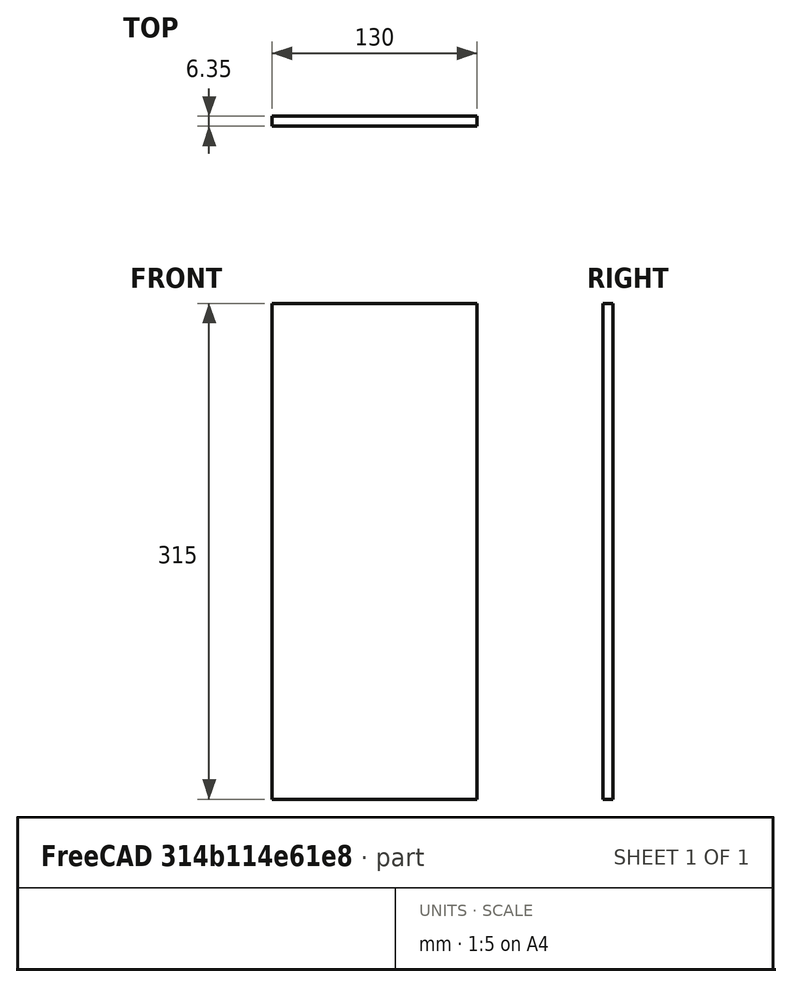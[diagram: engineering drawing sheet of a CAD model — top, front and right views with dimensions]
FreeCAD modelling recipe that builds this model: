
FCSTD DOCUMENT  (FreeCAD 1.0R39109 (Git))
Label: Integrated PiTrac
License: All rights reserved
LicenseURL: http://en.wikipedia.org/wiki/All_rights_reserved
objects: App::Link×14, App::Part×2, Sketcher::SketchObject×1, PartDesign::Pad×1, PartDesign::Body×1
note: 6 computed .brp shape members not serialized (recipe doc carries the construction recipe); baked Part::Feature solids carry a one-line shape summary decoded from their .brp
EXTERNAL_REF file=../Master Document.FCStd obj=Spreadsheet
EXTERNAL_REF file=../PiTracComputeBoard/PiTracComputeBoard.FCStd obj=p2AP_PCBModel
EXTERNAL_REF file=../Tower/Tower.FCStd obj=Part
EXTERNAL_REF file=../Pi-Camera-Mounts/Camera Mount - Bottom.FCStd obj=Part
EXTERNAL_REF file=../LED-Array-Strobe-Light-Mount/LED Light Mount.FCStd obj=Part
EXTERNAL_REF file=Pi HQ Camera.FCStd obj=Raspberry_Pi_HQ_Camera_with_cs_mount_lens_v3
EXTERNAL_REF file=Cree LED Lens.FCStd obj=Scale
EXTERNAL_REF file=../Pi-Camera-Mounts/Camera Mount - Top Variation (Cam1).FCStd obj=Part
EXTERNAL_REF file=../Pi-Camera-Light-Filter-Holder/Pi Cam Filter Holder v1.00.FCStd obj=Part
EXTERNAL_REF file=../BaseBox/BaseBox.FCStd obj=Part
EXTERNAL_REF file=LRS-150 Meanwell.FCStd obj=LRS_150
EXTERNAL_REF file=C14 Panel Mount Power Plug Adapter w Fuse - JR-101-1F.FCStd obj=JR_101_1F
EXTERNAL_REF file=../CaseCover/CaseCover.FCStd obj=Part

FEATURE [App::Part] Part  label="Integrated Part"
  Origin = -> Origin
FEATURE [App::Link] Link  label="Monitor Chassis Parameters"
  LinkPlacement = pos=(-5.9,7.03335e-07,0) rot=(0,0,1;0rad)
  LinkedObject = -> <external ../Master Document.FCStd>#Spreadsheet
  Placement = pos=(-5.9,7.03335e-07,0) rot=(0,0,1;0rad)
FEATURE [App::Link] Link002  label="p2AP-PCBModel"
  LinkPlacement = pos=(-49.1,-7.80001,20.1) rot=(1,0,0;1.5708rad)
  LinkedObject = -> <external ../PiTracComputeBoard/PiTracComputeBoard.FCStd>#p2AP_PCBModel
  Placement = pos=(-49.1,-7.80001,20.1) rot=(1,0,0;1.5708rad)
FEATURE [App::Link] Link003  label="Tower Part"
  LinkPlacement = pos=(1.5,3.6,0) rot=(0,0,1;0rad)
  LinkedObject = -> <external ../Tower/Tower.FCStd>#Part
  Placement = pos=(1.5,3.6,0) rot=(0,0,1;0rad)
FEATURE [App::Link] Link004  label="Botom Camera Mount Object"
  LinkPlacement = pos=(1.5,11.8,24.2) rot=(1,0,0;1.5708rad)
  LinkedObject = -> <external ../Pi-Camera-Mounts/Camera Mount - Bottom.FCStd>#Part
  Placement = pos=(1.5,11.8,24.2) rot=(1,0,0;1.5708rad)
FEATURE [App::Link] Link005  label="LED Light Mount Object"
  LinkPlacement = pos=(1.1,50.9,87.4) rot=(1,0,0;1.5708rad)
  LinkedObject = -> <external ../LED-Array-Strobe-Light-Mount/LED Light Mount.FCStd>#Part
  Placement = pos=(1.1,50.9,87.4) rot=(1,0,0;1.5708rad)
FEATURE [App::Link] Link006  label="Bottom Raspberry Pi HQ Camera with cs mount lens v014"
  LinkPlacement = pos=(-17.4,39.4031,23.6917) rot=(1,0,0;0.261799rad)
  LinkedObject = -> <external Pi HQ Camera.FCStd>#Raspberry_Pi_HQ_Camera_with_cs_mount_lens_v3
  Placement = pos=(-17.4,39.4031,23.6917) rot=(1,0,0;0.261799rad)
FEATURE [App::Link] Link007  label="LED Lens Scale"
  LinkPlacement = pos=(0,45.6236,128.978) rot=(1,0,0;0.261799rad)
  LinkedObject = -> <external Cree LED Lens.FCStd>#Scale
  Placement = pos=(0,45.6236,128.978) rot=(1,0,0;0.261799rad)
FEATURE [App::Link] Link008  label="Camera Mount - Top Object"
  LinkPlacement = pos=(15.7,56.8,199.2) rot=(1,0,0;1.5708rad)
  LinkedObject = -> <external ../Pi-Camera-Mounts/Camera Mount - Top Variation (Cam1).FCStd>#Part
  Placement = pos=(15.7,56.8,199.2) rot=(1,0,0;1.5708rad)
FEATURE [App::Link] Link009  label="Raspberry Pi HQ Camera with cs mount lens v014"
  LinkPlacement = pos=(-17.6,24.9301,203.909) rot=(-1,0,0;0.523599rad)
  LinkedObject = -> <external Pi HQ Camera.FCStd>#Raspberry_Pi_HQ_Camera_with_cs_mount_lens_v3
  Placement = pos=(-17.6,24.9301,203.909) rot=(-1,0,0;0.523599rad)
FEATURE [App::Link] Link010  label="Filter Holder Part"
  LinkPlacement = pos=(0.6,83.4834,56.5158) rot=(1,0,0;0.261799rad)
  LinkedObject = -> <external ../Pi-Camera-Light-Filter-Holder/Pi Cam Filter Holder v1.00.FCStd>#Part
  Placement = pos=(0.6,83.4834,56.5158) rot=(1,0,0;0.261799rad)
FEATURE [App::Link] Link011  label="BaseBox Part"
  LinkPlacement = pos=(101.6,36.6,-51) rot=(0,0,1;3.14159rad)
  LinkedObject = -> <external ../BaseBox/BaseBox.FCStd>#Part
  Placement = pos=(101.6,36.6,-51) rot=(0,0,1;3.14159rad)
FEATURE [App::Link] Link012  label="LRS-154"
  LinkPlacement = pos=(18,9.4,-50.9) rot=(-0.57735,0.57735,0.57735;4.18879rad)
  LinkedObject = -> <external LRS-150 Meanwell.FCStd>#LRS_150
  Placement = pos=(18,9.4,-50.9) rot=(-0.57735,0.57735,0.57735;4.18879rad)
FEATURE [Sketcher::SketchObject] Sketch  label="Shank Shield Sketch"
  ArcFitTolerance = 1e-06
  AttachmentSupport = -> [XZ_Plane002]
  FullyConstrained = false
  MakeInternals = false
  MapMode = 5
  Placement = pos=(0,0,0) rot=(1,0,0;1.5708rad)
  expr: Constraints[8] = <<Monitor Chassis Parameters>>.GSShankShieldWidth
  expr: Constraints[9] = <<Monitor Chassis Parameters>>.GSShankShieldHeight
  sketch-geometry (4):
    g0: LineSegment StartX=68.4149 StartY=-76.5925 StartZ=0 EndX=68.4149 EndY=238.407 EndZ=0
    g1: LineSegment StartX=68.4149 StartY=238.407 StartZ=0 EndX=-61.5851 EndY=238.407 EndZ=0
    g2: LineSegment StartX=-61.5851 StartY=238.407 StartZ=0 EndX=-61.5851 EndY=-76.5925 EndZ=0
    g3: LineSegment StartX=-61.5851 StartY=-76.5925 StartZ=0 EndX=68.4149 EndY=-76.5925 EndZ=0
  constraints (10):
    c: Coincident(g0,g1)
    c: Coincident(g1,g2)
    c: Coincident(g2,g3)
    c: Coincident(g3,g0)
    c: Vertical(g0)
    c: Vertical(g2)
    c: Horizontal(g1)
    c: Horizontal(g3)
    c: DistanceX(g1,g0) = 130
    c: DistanceY(g0,g0) = 315
FEATURE [PartDesign::Pad] Pad  label="Shank Shield Pad"
  Direction = (0,-1,2e-16)
  Length = 6.35
  Length2 = 10
  Placement = pos=(0,0,0) rot=(1,0,0;1.5708rad)
  Profile = -> Sketch
  ReferenceAxis = -> Sketch [N_Axis]
  Suppressed = false
  Type = 0
  expr: Length = <<Monitor Chassis Parameters>>.GSShankShieldThickness
FEATURE [PartDesign::Body] Body  label="Shank Shield Body"
  AllowCompound = false
  Group = -> [Sketch,Pad]
  Origin = -> Origin002
  Tip = -> Pad
FEATURE [App::Part] Part001  label="Shank Shield Part"
  Group = -> [Body]
  Origin = -> Origin001
  Placement = pos=(0,112.4,25.5) rot=(0,0,1;0rad)
FEATURE [App::Link] Link013  label="JR-101-1F008"
  LinkPlacement = pos=(-98.4001,76.6999,-31.4001) rot=(0.57735,-0.57735,-0.57735;2.0944rad)
  LinkedObject = -> <external C14 Panel Mount Power Plug Adapter w Fuse - JR-101-1F.FCStd>#JR_101_1F
  Placement = pos=(-98.4001,76.6999,-31.4001) rot=(0.57735,-0.57735,-0.57735;2.0944rad)
FEATURE [App::Link] Link014  label="Case Cover Part"
  LinkPlacement = pos=(2.9,27.2,-5.1) rot=(0,0,1;3.14159rad)
  LinkedObject = -> <external ../CaseCover/CaseCover.FCStd>#Part
  Placement = pos=(2.9,27.2,-5.1) rot=(0,0,1;3.14159rad)

RESOLVED EXTERNAL PARTS (link-assembly join: the EXTERNAL_REF files above that resolve inside this repo's crawl, each included once):
---- part ../BaseBox/BaseBox.FCStd = doc fcstd_369560cff5c8 (88262 chars; too large to inline — full recipe in that document) ----
---- part ../CaseCover/CaseCover.FCStd = doc fcstd_a5773d0cd6bc ----
FCSTD DOCUMENT  (FreeCAD 1.0R39109 (Git))
Label: CaseCover
License: All rights reserved
LicenseURL: http://en.wikipedia.org/wiki/All_rights_reserved
objects: Sketcher::SketchObject×17, PartDesign::Pad×9, PartDesign::Plane×8, PartDesign::Pocket×8, PartDesign::LinearPattern×3, PartDesign::Mirrored×2, PartDesign::Body×2, App::Link×1, App::Part×1
note: 105 computed .brp shape members not serialized (recipe doc carries the construction recipe); baked Part::Feature solids carry a one-line shape summary decoded from their .brp
EXTERNAL_REF file=../Master Document.FCStd obj=Spreadsheet

FEATURE [App::Link] Link  label="Monitor Chassis Parameters"
  LinkedObject = -> <external ../Master Document.FCStd>#Spreadsheet
FEATURE [Sketcher::SketchObject] Sketch  label="Lower Case Wall Base Sketch"
  ArcFitTolerance = 1e-06
  AttachmentSupport = -> [XY_Plane001]
  FullyConstrained = true
  MakeInternals = false
  MapMode = 5
  expr: Constraints[11] = 0.5 * <<Monitor Chassis Parameters>>.GSCaseWallInnerDepth
  expr: Constraints[12] = <<Monitor Chassis Parameters>>.GSCaseWallInnerWidth
  expr: Constraints[13] = <<Monitor Chassis Parameters>>.GSCaseWallThickness
  expr: Constraints[14] = 0.5 * <<Monitor Chassis Parameters>>.GSCaseWallInnerWidth
  expr: Constraints[23] = <<Monitor Chassis Parameters>>.GSCaseWallThickness
  expr: Constraints[24] = <<Monitor Chassis Parameters>>.GSCaseWallThickness
  expr: Constraints[9] = <<Monitor Chassis Parameters>>.GSCaseWallInnerDepth
  sketch-geometry (8):
    g0: LineSegment StartX=62.3 StartY=64.5 StartZ=0 EndX=-62.3 EndY=64.5 EndZ=0
    g1: LineSegment StartX=-62.3 StartY=64.5 StartZ=0 EndX=-62.3 EndY=-61.5 EndZ=0
    g2: LineSegment StartX=-62.3 StartY=-61.5 StartZ=0 EndX=-59.3 EndY=-61.5 EndZ=0
    g3: LineSegment StartX=-59.3 StartY=-61.5 StartZ=0 EndX=-59.3 EndY=61.5 EndZ=0
    g4: LineSegment StartX=59.3 StartY=61.5 StartZ=0 EndX=59.3 EndY=-61.5 EndZ=0
    g5: LineSegment StartX=59.3 StartY=-61.5 StartZ=0 EndX=62.3 EndY=-61.5 EndZ=0
    g6: LineSegment StartX=-59.3 StartY=61.5 StartZ=0 EndX=59.3 EndY=61.5 EndZ=0
    g7: LineSegment StartX=62.3 StartY=-61.5 StartZ=0 EndX=62.3 EndY=64.5 EndZ=0
  constraints (26):
    c: Horizontal(g0)
    c: Coincident(g1,g2)
    c: Coincident(g2,g3)
    c: Vertical(g1)
    c: Vertical(g3)
    c: Horizontal(g2)
    c: Coincident(g4,g5)
    c: Horizontal(g5)
    c: Vertical(g4)
    c: DistanceY(g2,g3) = 123
    c: Horizontal(g2,g4)
    c: DistanceY(g-1,g4) = 61.5
    c: DistanceX(g3,g4) = 118.6
    c: DistanceX(g0,g3) = 3
    c: DistanceX(g-1,g4) = 59.3
    c: Vertical(g0,g1)
    c: Horizontal(g0,g1)
    c: Coincident(g6,g3)
    c: Coincident(g6,g4)
    c: Horizontal(g6)
    c: PointOnObject(g7,g5)
    c: Coincident(g7,g0)
    c: Vertical(g7)
    c: DistanceY(g4,g0) = 3
    c: DistanceX(g4,g0) = 3
    c: Vertical(g7,g5)
FEATURE [PartDesign::Pad] Pad  label="Lower Case Wall Base Pad"
  Direction = (0,0,1)
  Length = 110
  Length2 = 10
  Profile = -> Sketch
  ReferenceAxis = -> Sketch [N_Axis]
  Suppressed = false
  Type = 0
  expr: Length = <<Monitor Chassis Parameters>>.GSLowerCaseHeight
FEATURE [Sketcher::SketchObject] Sketch001  label="Left Lower Case Corner Gusset Sketch"
  ArcFitTolerance = 1e-06
  AttachmentSupport = -> [XY_Plane001]
  FullyConstrained = true
  MakeInternals = false
  MapMode = 5
  expr: Constraints[6] = 0.5 * <<Monitor Chassis Parameters>>.GSCaseWallInnerWidth
  expr: Constraints[7] = 0.5 * <<Monitor Chassis Parameters>>.GSCaseWallInnerDepth
  expr: Constraints[8] = <<Monitor Chassis Parameters>>.GSCaseWallCornerGussetLength
  sketch-geometry (3):
    g0: LineSegment StartX=-59.3 StartY=59.5 StartZ=0 EndX=-57.3 EndY=61.5 EndZ=0
    g1: LineSegment StartX=-57.3 StartY=61.5 StartZ=0 EndX=-59.3 EndY=61.5 EndZ=0
    g2: LineSegment StartX=-59.3 StartY=61.5 StartZ=0 EndX=-59.3 EndY=59.5 EndZ=0
  constraints (9):
    c: Coincident(g1,g0)
    c: Horizontal(g1)
    c: Coincident(g2,g1)
    c: Coincident(g2,g0)
    c: Vertical(g2)
    c: Angle(g0) = 0.785398
    c: DistanceX(g1,g-1) = 59.3
    c: DistanceY(g-1,g1) = 61.5
    c: DistanceY(g0,g1) = 2
FEATURE [PartDesign::Pad] Pad001  label="Left Lower Case Corner Gusset Pad"
  BaseFeature = -> Pad
  Direction = (0,0,1)
  Length = 96
  Length2 = 10
  Profile = -> Sketch001
  ReferenceAxis = -> Sketch001 [N_Axis]
  Suppressed = false
  Type = 0
  expr: Length = <<Monitor Chassis Parameters>>.GSLowerCaseHeight - <<Monitor Chassis Parameters>>.GSCaseConnectionWallHeight
FEATURE [PartDesign::Mirrored] Mirrored  label="Right Lower Case Corner Gusset Mirror"
  BaseFeature = -> Pad001
  MirrorPlane = -> YZ_Plane001
  Originals = -> [Pad001]
  Suppressed = false
  TransformMode = 0
FEATURE [PartDesign::Plane] DatumPlane  label="Back of Cover DatumPlane"
  AttachmentOffset = pos=(0,0,-64.5) rot=(0,0,1;0rad)
  AttachmentSupport = -> [XZ_Plane001]
  Length = 151.203
  MapMode = 5
  Placement = pos=(0,64.5,-1.43e-14) rot=(1,0,0;1.5708rad)
  ResizeMode = 0
  Width = 168.603
  expr: .AttachmentOffset.Base.z = -(0.5 * <<Monitor Chassis Parameters>>.GSCaseWallInnerDepth + <<Monitor Chassis Parameters>>.GSCaseWallThickness)
FEATURE [PartDesign::Plane] DatumPlane001  label="Front of Cover DatumPlane"
  AttachmentOffset = pos=(0,0,61.5) rot=(0,0,1;0rad)
  AttachmentSupport = -> [XZ_Plane001]
  Length = 151.203
  MapMode = 5
  Placement = pos=(0,-61.5,1.37e-14) rot=(1,0,0;1.5708rad)
  ResizeMode = 0
  Width = 168.603
  expr: .AttachmentOffset.Base.z = 0.5 * <<Monitor Chassis Parameters>>.GSCaseWallInnerDepth
FEATURE [Sketcher::SketchObject] Sketch003  label="Cover Front Lower Crossbeam Sketch"
  ArcFitTolerance = 1e-06
  AttachmentSupport = -> [DatumPlane001]
  FullyConstrained = true
  MakeInternals = false
  MapMode = 5
  Placement = pos=(0,-61.5,1.37e-14) rot=(1,0,0;1.5708rad)
  expr: Constraints[10] = <<Monitor Chassis Parameters>>.GSCaseWallInnerWidth
  expr: Constraints[11] = 0.5 * <<Monitor Chassis Parameters>>.GSCaseWallInnerWidth
  sketch-geometry (4):
    g0: LineSegment StartX=59.3 StartY=10 StartZ=0 EndX=-59.3 EndY=10 EndZ=0
    g1: LineSegment StartX=-59.3 StartY=10 StartZ=0 EndX=-59.3 EndY=0 EndZ=0
    g2: LineSegment StartX=-59.3 StartY=0 StartZ=0 EndX=59.3 EndY=0 EndZ=0
    g3: LineSegment StartX=59.3 StartY=0 StartZ=0 EndX=59.3 EndY=10 EndZ=0
  constraints (12):
    c: Coincident(g0,g1)
    c: Coincident(g1,g2)
    c: Coincident(g2,g3)
    c: Coincident(g3,g0)
    c: Horizontal(g0)
    c: Horizontal(g2)
    c: Vertical(g1)
    c: Vertical(g3)
    c: Horizontal(g2,g-1)
    c: DistanceY(g2,g0) = 10
    c: DistanceX(g0,g0) = 118.6
    c: DistanceX(g-1,g2) = 59.3
FEATURE [PartDesign::Pad] Pad002  label="Cover Front Lower Crossbeam Pad"
  BaseFeature = -> Mirrored
  Direction = (0,-1,2e-16)
  Length = 3
  Length2 = 10
  Profile = -> Sketch003
  ReferenceAxis = -> Sketch003 [N_Axis]
  Reversed = true
  Suppressed = false
  Type = 0
  expr: Length = <<Monitor Chassis Parameters>>.GSCaseWallThickness
FEATURE [Sketcher::SketchObject] Sketch004  label="Cover Lower Connection Side Tabs Sketch"
  ArcFitTolerance = 1e-06
  AttachmentSupport = -> [DatumPlane001]
  FullyConstrained = true
  MakeInternals = false
  MapMode = 5
  Placement = pos=(0,-61.5,1.37e-14) rot=(1,0,0;1.5708rad)
  expr: Constraints[13] = <<Monitor Chassis Parameters>>.GSCaseConnectionWallThickness
  expr: Constraints[15] = <<Monitor Chassis Parameters>>.GSCaseWallInnerWidth
  expr: Constraints[3] = <<Monitor Chassis Parameters>>.GSLowerCaseHeight + 0.5 * <<Monitor Chassis Parameters>>.GSCaseConnectionWallHeight
  expr: Constraints[4] = <<Monitor Chassis Parameters>>.GSCaseConnectionWallHeight
  expr: Constraints[5] = 0.5 * <<Monitor Chassis Parameters>>.GSCaseWallInnerWidth
  expr: Constraints[6] = <<Monitor Chassis Parameters>>.GSCaseConnectionWallThickness
  sketch-geometry (8):
    g0: LineSegment StartX=-57.3 StartY=117 StartZ=0 EndX=-59.3 EndY=117 EndZ=0
    g1: LineSegment StartX=-59.3 StartY=117 StartZ=0 EndX=-59.3 EndY=100 EndZ=0
    g2: LineSegment StartX=57.3 StartY=103 StartZ=0 EndX=57.3 EndY=117 EndZ=0
    g3: LineSegment StartX=57.3 StartY=117 StartZ=0 EndX=59.3 EndY=117 EndZ=0
    g4: LineSegment StartX=59.3 StartY=117 StartZ=0 EndX=59.3 EndY=100 EndZ=0
    g5: LineSegment StartX=-57.3 StartY=117 StartZ=0 EndX=-57.3 EndY=103 EndZ=0
    g6: LineSegment StartX=-59.3 StartY=100 StartZ=0 EndX=-57.3 EndY=103 EndZ=0
    g7: LineSegment StartX=59.3 StartY=100 StartZ=0 EndX=57.3 EndY=103 EndZ=0
  constraints (24):
    c: Coincident(g0,g1)
    c: Vertical(g1)
    c: Horizontal(g0)
    c: DistanceY(g-1,g0) = 117
    c: DistanceY(g5,g0) = 14
    c: DistanceX(g1,g-1) = 59.3
    c: DistanceX(g1,g5) = 2
    c: Coincident(g2,g3)
    c: Coincident(g3,g4)
    c: Vertical(g2)
    c: Vertical(g4)
    c: Horizontal(g3)
    c: Horizontal(g0,g2)
    c: DistanceX(g2,g3) = 2
    c: Horizontal(g5,g2)
    c: DistanceX(g0,g3) = 118.6
    c: Coincident(g5,g0)
    c: Vertical(g5)
    c: Coincident(g6,g1)
    c: Coincident(g6,g5)
    c: DistanceY(g1,g5) = 3
    c: Coincident(g7,g4)
    c: Coincident(g7,g2)
    c: Horizontal(g4,g1)
FEATURE [PartDesign::Pad] Pad003  label="Cover Lower Connection Side Tabs Pad"
  BaseFeature = -> Pad002
  Direction = (0,-1,2e-16)
  Length = 123
  Length2 = 10
  Profile = -> Sketch004
  ReferenceAxis = -> Sketch004 [N_Axis]
  Reversed = true
  Suppressed = false
  Type = 0
  expr: Length = <<Monitor Chassis Parameters>>.GSCaseWallInnerDepth
FEATURE [Sketcher::SketchObject] Sketch006  label="Upper Case Wall Base Sketch"
  ArcFitTolerance = 1e-06
  AttachmentSupport = -> [XY_Plane002]
  FullyConstrained = true
  MakeInternals = false
  MapMode = 5
  expr: Constraints[16] = <<Monitor Chassis Parameters>>.GSCaseWallThickness
  expr: Constraints[17] = <<Monitor Chassis Parameters>>.GSCaseWallThickness
  expr: Constraints[18] = <<Monitor Chassis Parameters>>.GSCaseWallThickness
  expr: Constraints[5] = <<Monitor Chassis Parameters>>.GSCaseWallInnerDepth
  expr: Constraints[7] = 0.5 * <<Monitor Chassis Parameters>>.GSCaseWallInnerDepth
  expr: Constraints[8] = 0.5 * <<Monitor Chassis Parameters>>.GSCaseWallInnerWidth
  expr: Constraints[9] = <<Monitor Chassis Parameters>>.GSCaseWallInnerWidth
  sketch-geometry (8):
    g0: LineSegment StartX=62.3 StartY=64.5 StartZ=0 EndX=-62.3 EndY=64.5 EndZ=0
    g1: LineSegment StartX=-62.3 StartY=-61.5 StartZ=0 EndX=-59.3 EndY=-61.5 EndZ=0
    g2: LineSegment StartX=-59.3 StartY=-61.5 StartZ=0 EndX=-59.3 EndY=61.5 EndZ=0
    g3: LineSegment StartX=59.3 StartY=61.5 StartZ=0 EndX=59.3 EndY=-61.5 EndZ=0
    g4: LineSegment StartX=-62.3 StartY=64.5 StartZ=0 EndX=-62.3 EndY=-61.5 EndZ=0
    g5: LineSegment StartX=-59.3 StartY=61.5 StartZ=0 EndX=59.3 EndY=61.5 EndZ=0
    g6: LineSegment StartX=62.3 StartY=64.5 StartZ=0 EndX=62.3 EndY=-61.5 EndZ=0
    g7: LineSegment StartX=59.3 StartY=-61.5 StartZ=0 EndX=62.3 EndY=-61.5 EndZ=0
  constraints (24):
    c: Horizontal(g0)
    c: Coincident(g1,g2)
    c: Vertical(g2)
    c: Horizontal(g1)
    c: Vertical(g3)
    c: DistanceY(g1,g2) = 123
    c: Horizontal(g1,g3)
    c: DistanceY(g-1,g3) = 61.5
    c: DistanceX(g2,g-1) = 59.3
    c: DistanceX(g2,g3) = 118.6
    c: Coincident(g4,g0)
    c: Coincident(g4,g1)
    c: Vertical(g4)
    c: Coincident(g5,g2)
    c: Coincident(g5,g3)
    c: Horizontal(g5)
    c: DistanceX(g0,g2) = 3
    c: DistanceY(g2,g0) = 3
    c: DistanceX(g3,g0) = 3
    c: Coincident(g6,g0)
    c: Vertical(g6)
    c: Coincident(g7,g3)
    c: Coincident(g7,g6)
    c: Horizontal(g3,g6)
FEATURE [PartDesign::Pad] Pad004  label="Upper Case Wall Base Pad"
  Direction = (0,0,1)
  Length = 153
  Length2 = 10
  Profile = -> Sketch006
  ReferenceAxis = -> Sketch006 [N_Axis]
  Suppressed = false
  Type = 0
  expr: Length = <<Monitor Chassis Parameters>>.GSUpperCaseHeight
FEATURE [PartDesign::Plane] DatumPlane002  label="Case Top DatumPlane"
  AttachmentOffset = pos=(0,0,153) rot=(0,0,1;0rad)
  AttachmentSupport = -> [XY_Plane002]
  Length = 149.66
  MapMode = 5
  Placement = pos=(0,0,153) rot=(0,0,1;0rad)
  ResizeMode = 0
  Width = 151.06
  expr: .AttachmentOffset.Base.z = <<Monitor Chassis Parameters>>.GSUpperCaseHeight
FEATURE [Sketcher::SketchObject] Sketch007  label="Case Cover Top Sketch"
  ArcFitTolerance = 1e-06
  AttachmentSupport = -> [DatumPlane002]
  FullyConstrained = true
  MakeInternals = false
  MapMode = 5
  Placement = pos=(0,0,153) rot=(0,0,1;0rad)
  expr: Constraints[10] = <<Monitor Chassis Parameters>>.GSCaseWallInnerDepth + <<Monitor Chassis Parameters>>.GSCaseWallThickness
  expr: Constraints[11] = 0.5 * (<<Monitor Chassis Parameters>>.GSCaseWallInnerDepth + 2 * <<Monitor Chassis Parameters>>.GSCaseWallThickness)
  expr: Constraints[8] = <<Monitor Chassis Parameters>>.GSCaseWallInnerWidth + 2 * <<Monitor Chassis Parameters>>.GSCaseWallThickness
  expr: Constraints[9] = 0.5 * <<Monitor Chassis Parameters>>.GSCaseWallInnerWidth + <<Monitor Chassis Parameters>>.GSCaseWallThickness
  sketch-geometry (4):
    g0: LineSegment StartX=-62.3 StartY=64.5 StartZ=0 EndX=-62.3 EndY=-61.5 EndZ=0
    g1: LineSegment StartX=-62.3 StartY=-61.5 StartZ=0 EndX=62.3 EndY=-61.5 EndZ=0
    g2: LineSegment StartX=62.3 StartY=-61.5 StartZ=0 EndX=62.3 EndY=64.5 EndZ=0
    g3: LineSegment StartX=62.3 StartY=64.5 StartZ=0 EndX=-62.3 EndY=64.5 EndZ=0
  constraints (12):
    c: Coincident(g0,g1)
    c: Coincident(g1,g2)
    c: Coincident(g2,g3)
    c: Coincident(g3,g0)
    c: Vertical(g0)
    c: Vertical(g2)
    c: Horizontal(g1)
    c: Horizontal(g3)
    c: DistanceX(g0,g2) = 124.6
    c: DistanceX(g0,g-1) = 62.3
    c: DistanceY(g0,g0) = 126
    c: DistanceY(g-1,g0) = 64.5
FEATURE [Sketcher::SketchObject] Sketch008  label="Left Upper Case Corner Gusset Sketch"
  ArcFitTolerance = 1e-06
  AttachmentSupport = -> [DatumPlane002]
  FullyConstrained = true
  MakeInternals = false
  MapMode = 5
  Placement = pos=(0,0,153) rot=(0,0,1;0rad)
  expr: Constraints[6] = 0.5 * <<Monitor Chassis Parameters>>.GSCaseWallInnerWidth
  expr: Constraints[7] = 0.5 * <<Monitor Chassis Parameters>>.GSCaseWallInnerDepth
  sketch-geometry (3):
    g0: LineSegment StartX=-59.3 StartY=59.5 StartZ=0 EndX=-57.3 EndY=61.5 EndZ=0
    g1: LineSegment StartX=-57.3 StartY=61.5 StartZ=0 EndX=-59.3 EndY=61.5 EndZ=0
    g2: LineSegment StartX=-59.3 StartY=61.5 StartZ=0 EndX=-59.3 EndY=59.5 EndZ=0
  constraints (9):
    c: Coincident(g1,g0)
    c: Horizontal(g1)
    c: Coincident(g2,g1)
    c: Coincident(g2,g0)
    c: Vertical(g2)
    c: Angle(g0) = 0.785398
    c: DistanceX(g1,g-1) = 59.3
    c: DistanceY(g-1,g1) = 61.5
    c: DistanceY(g0,g1) = 2
FEATURE [PartDesign::Pad] Pad005  label="Left Upper Case Corner Gusset Pad"
  BaseFeature = -> Pad004
  Direction = (0,0,1)
  Length = 139
  Length2 = 10
  Profile = -> Sketch008
  ReferenceAxis = -> Sketch008 [N_Axis]
  Reversed = true
  Suppressed = false
  Type = 0
  expr: Length = <<Monitor Chassis Parameters>>.GSUpperCaseHeight - <<Monitor Chassis Parameters>>.GSCaseConnectionWallHeight
FEATURE [PartDesign::Mirrored] Mirrored001  label="Right Upper Case Corner Gusset Mirrored"
  BaseFeature = -> Pad005
  MirrorPlane = -> Sketch008 [V_Axis]
  Originals = -> [Pad005]
  Suppressed = false
  TransformMode = 0
FEATURE [PartDesign::Pad] Pad006  label="Case Cover Top Pad"
  BaseFeature = -> Mirrored001
  Direction = (0,0,1)
  Length = 3
  Length2 = 10
  Profile = -> Sketch007
  ReferenceAxis = -> Sketch007 [N_Axis]
  Suppressed = false
  Type = 0
  expr: Length = <<Monitor Chassis Parameters>>.GSCaseWallThickness
FEATURE [PartDesign::Plane] DatumPlane003  label="Lower Cover Right Side DatumPlane"
  AttachmentOffset = pos=(0,0,62.3) rot=(0,0,1;0rad)
  AttachmentSupport = -> [YZ_Plane001]
  Length = 152.752
  MapMode = 5
  Placement = pos=(62.3,0,0) rot=(0.57735,0.57735,0.57735;2.0944rad)
  ResizeMode = 0
  Width = 168.752
  expr: .AttachmentOffset.Base.z = 0.5 * <<Monitor Chassis Parameters>>.GSCaseWallInnerWidth + <<Monitor Chassis Parameters>>.GSCaseWallThickness
FEATURE [Sketcher::SketchObject] Sketch009  label="Lower Cover Cooling Slot Base Sketch"
  ArcFitTolerance = 1e-06
  AttachmentSupport = -> [DatumPlane003]
  FullyConstrained = true
  MakeInternals = false
  MapMode = 5
  Placement = pos=(62.3,0,0) rot=(0.57735,0.57735,0.57735;2.0944rad)
  expr: Constraints[13] = <<Monitor Chassis Parameters>>.GSTowerSideCoolingSlotOffsetFromEdge
  expr: Constraints[2] = <<Monitor Chassis Parameters>>.GSTowerCoolingSlotEndOffset
  expr: Constraints[5] = <<Monitor Chassis Parameters>>.GSLowerCaseHeight + <<Monitor Chassis Parameters>>.GSUpperCaseHeight - <<Monitor Chassis Parameters>>.GSTowerCoolingSlotEndOffset
  expr: Constraints[6] = <<Monitor Chassis Parameters>>.GSTowerCoolingSlotWidth
  sketch-geometry (4):
    g0: LineSegment StartX=-46 StartY=20 StartZ=0 EndX=-46 EndY=243 EndZ=0
    g1: LineSegment StartX=-42 StartY=243 StartZ=0 EndX=-42 EndY=20 EndZ=0
    g2: ArcOfCircle CenterX=-44 CenterY=20 CenterZ=0 NormalX=0 NormalY=0 NormalZ=1 AngleXU=0 Radius=2 StartAngle=3.14159 EndAngle=6.28319
    g3: ArcOfCircle CenterX=-44 CenterY=243 CenterZ=0 NormalX=0 NormalY=0 NormalZ=1 AngleXU=0 Radius=2 StartAngle=0 EndAngle=3.14159
  constraints (14):
    c: Vertical(g0)
    c: Vertical(g1)
    c: DistanceY(g-1,g1) = 20
    c: Horizontal(g0,g1)
    c: Horizontal(g1,g0)
    c: DistanceY(g-1,g1) = 243
    c: DistanceX(g0,g1) = 4
    c: Coincident(g2,g0)
    c: Coincident(g2,g1)
    c: Horizontal(g2,g1)
    c: Coincident(g3,g0)
    c: Coincident(g3,g1)
    c: Horizontal(g3,g1)
    c: DistanceX(g1,g-1) = 42
FEATURE [PartDesign::Pocket] Pocket001  label="Lower Cover Cooling Slot Base Pocket"
  BaseFeature = -> Pad003
  Direction = (-1,0,0)
  Length = 5
  Length2 = 5
  Profile = -> Sketch009
  ReferenceAxis = -> Sketch009 [N_Axis]
  Suppressed = false
  Type = 1
FEATURE [PartDesign::LinearPattern] LinearPattern  label="Lower Cover Cooling Slot Base LinearPattern"
  BaseFeature = -> Pocket001
  Direction = -> Sketch009 [H_Axis]
  Length = 90
  Mode = 0
  Occurrences = 5
  Offset = 22.5
  Originals = -> [Pocket001]
  Suppressed = false
  TransformMode = 0
FEATURE [PartDesign::Plane] DatumPlane004  label="Upper Cover Right Side DatumPlane"
  AttachmentOffset = pos=(0,0,62.3) rot=(0,0,1;0rad)
  AttachmentSupport = -> [YZ_Plane002]
  Length = 161.319
  MapMode = 5
  Placement = pos=(62.3,0,0) rot=(0.57735,0.57735,0.57735;2.0944rad)
  ResizeMode = 0
  Width = 282.833
  expr: .AttachmentOffset.Base.z = 0.5 * <<Monitor Chassis Parameters>>.GSCaseWallInnerWidth + <<Monitor Chassis Parameters>>.GSCaseWallThickness
FEATURE [Sketcher::SketchObject] Sketch010  label="Upper Cover Cooling Slot Base Sketch"
  ArcFitTolerance = 1e-06
  AttachmentSupport = -> [DatumPlane004]
  FullyConstrained = false
  MakeInternals = false
  MapMode = 5
  Placement = pos=(62.3,0,0) rot=(0.57735,0.57735,0.57735;2.0944rad)
  expr: Constraints[12] = <<Monitor Chassis Parameters>>.GSTowerSideCoolingSlotOffsetFromEdge
  expr: Constraints[4] = <<Monitor Chassis Parameters>>.GSUpperCaseHeight - <<Monitor Chassis Parameters>>.GSTowerCoolingSlotEndOffset
  expr: Constraints[5] = <<Monitor Chassis Parameters>>.GSTowerCoolingSlotWidth
  sketch-geometry (4):
    g0: LineSegment StartX=-46 StartY=-89.5276 StartZ=0 EndX=-46 EndY=133 EndZ=0
    g1: LineSegment StartX=-42 StartY=133 StartZ=0 EndX=-42 EndY=-89.5276 EndZ=0
    g2: ArcOfCircle CenterX=-44 CenterY=-89.5276 CenterZ=0 NormalX=0 NormalY=0 NormalZ=1 AngleXU=0 Radius=2 StartAngle=3.14159 EndAngle=6.28319
    g3: ArcOfCircle CenterX=-44 CenterY=133 CenterZ=0 NormalX=0 NormalY=0 NormalZ=1 AngleXU=0 Radius=2 StartAngle=0 EndAngle=3.14159
  constraints (13):
    c: Vertical(g0)
    c: Vertical(g1)
    c: Horizontal(g0,g1)
    c: Horizontal(g1,g0)
    c: DistanceY(g-1,g1) = 133
    c: DistanceX(g0,g1) = 4
    c: Coincident(g2,g0)
    c: Coincident(g2,g1)
    c: Horizontal(g2,g1)
    c: Coincident(g3,g0)
    c: Coincident(g3,g1)
    c: Horizontal(g3,g1)
    c: DistanceX(g1,g-1) = 42
FEATURE [PartDesign::Pocket] Pocket002  label="Upper Cover Cooling Slot Base Pocket"
  BaseFeature = -> Pad006
  Direction = (-1,0,0)
  Length = 5
  Length2 = 5
  Profile = -> Sketch010
  ReferenceAxis = -> Sketch010 [N_Axis]
  Suppressed = false
  Type = 1
FEATURE [PartDesign::LinearPattern] LinearPattern001  label="Upper Cover Cooling Slot Base LinearPattern"
  BaseFeature = -> Pocket002
  Direction = -> Sketch010 [H_Axis]
  Length = 90
  Mode = 0
  Occurrences = 5
  Offset = 22.5
  Originals = -> [Pocket002]
  Suppressed = false
  TransformMode = 0
FEATURE [Sketcher::SketchObject] Sketch011  label="Tower Top Cooling Slots Sketch"
  ArcFitTolerance = 1e-06
  AttachmentSupport = -> [Pad006]
  FullyConstrained = true
  MakeInternals = false
  MapMode = 5
  Placement = pos=(0,0,156) rot=(0,0,1;0rad)
  expr: Constraints[10] = 0.5 * <<Monitor Chassis Parameters>>.GSCaseWallInnerWidth - <<Monitor Chassis Parameters>>.GSTowerTopCoolingSlotOffsetFromEdge
  expr: Constraints[11] = 0.5 * <<Monitor Chassis Parameters>>.GSCaseWallInnerWidth - <<Monitor Chassis Parameters>>.GSTowerTopCoolingSlotOffsetFromEdge
  expr: Constraints[12] = <<Monitor Chassis Parameters>>.GSTowerCoolingSlotWidth
  expr: Constraints[13] = <<Monitor Chassis Parameters>>.GSTowerSideCoolingSlotOffsetFromEdge
  sketch-geometry (4):
    g0: LineSegment StartX=-45.3 StartY=-42 StartZ=0 EndX=45.3 EndY=-42 EndZ=0
    g1: LineSegment StartX=45.3 StartY=-46 StartZ=0 EndX=-45.3 EndY=-46 EndZ=0
    g2: ArcOfCircle CenterX=-45.3 CenterY=-44 CenterZ=0 NormalX=0 NormalY=0 NormalZ=1 AngleXU=0 Radius=2 StartAngle=1.5708 EndAngle=4.71239
    g3: ArcOfCircle CenterX=45.3 CenterY=-44 CenterZ=0 NormalX=0 NormalY=0 NormalZ=1 AngleXU=0 Radius=2 StartAngle=4.71239 EndAngle=7.85398
  constraints (14):
    c: Horizontal(g0)
    c: Horizontal(g1)
    c: Vertical(g0,g1)
    c: Vertical(g0,g1)
    c: Coincident(g2,g0)
    c: Coincident(g2,g1)
    c: Coincident(g3,g0)
    c: Coincident(g3,g1)
    c: Vertical(g0,g3)
    c: Vertical(g0,g2)
    c: DistanceX(g-1,g1) = 45.3
    c: DistanceX(g0,g-1) = 45.3
    c: DistanceY(g1,g0) = 4
    c: DistanceY(g0,g-1) = 42
FEATURE [PartDesign::Pocket] Pocket003  label="Case Top Cooling Slots Pocket"
  BaseFeature = -> LinearPattern001
  Direction = (0,0,-1)
  Length = 4
  Length2 = 5
  Profile = -> Sketch011
  ReferenceAxis = -> Sketch011 [N_Axis]
  Suppressed = false
  Type = 0
  expr: Length = <<Monitor Chassis Parameters>>.GSTowerFloorThickness
FEATURE [PartDesign::LinearPattern] LinearPattern002  label="Case Top Cooling Slots LinearPattern"
  BaseFeature = -> Pocket003
  Direction = -> Y_Axis002
  Length = 90
  Mode = 0
  Occurrences = 5
  Offset = 22.5
  Originals = -> [Pocket003]
  Suppressed = false
  TransformMode = 0
FEATURE [Sketcher::SketchObject] Sketch012  label="Lower Right Case Holes Sketch"
  ArcFitTolerance = 1e-06
  AttachmentSupport = -> [DatumPlane003]
  FullyConstrained = false
  MakeInternals = false
  MapMode = 5
  Placement = pos=(62.3,0,0) rot=(0.57735,0.57735,0.57735;2.0944rad)
  expr: Constraints[18] = <<Monitor Chassis Parameters>>.GSLowerRightSwitchHoleWidth
  expr: Constraints[19] = <<Monitor Chassis Parameters>>.GSLowerRightSwitchHoleLength
  expr: Constraints[8] = <<Monitor Chassis Parameters>>.GSLowerRightSwitchHoleWidth
  expr: Constraints[9] = <<Monitor Chassis Parameters>>.GSLowerRightSwitchHoleLength
  sketch-geometry (8):
    g0: LineSegment StartX=44.8307 StartY=95.724 StartZ=0 EndX=38.8307 EndY=95.724 EndZ=0
    g1: LineSegment StartX=38.8307 StartY=95.724 StartZ=0 EndX=38.8307 EndY=83.724 EndZ=0
    g2: LineSegment StartX=38.8307 StartY=83.724 StartZ=0 EndX=44.8307 EndY=83.724 EndZ=0
    g3: LineSegment StartX=44.8307 StartY=83.724 StartZ=0 EndX=44.8307 EndY=95.724 EndZ=0
    g4: LineSegment StartX=44.8307 StartY=68.6514 StartZ=0 EndX=38.8307 EndY=68.6514 EndZ=0
    g5: LineSegment StartX=38.8307 StartY=68.6514 StartZ=0 EndX=38.8307 EndY=56.6514 EndZ=0
    g6: LineSegment StartX=38.8307 StartY=56.6514 StartZ=0 EndX=44.8307 EndY=56.6514 EndZ=0
    g7: LineSegment StartX=44.8307 StartY=56.6514 StartZ=0 EndX=44.8307 EndY=68.6514 EndZ=0
  constraints (21):
    c: Coincident(g0,g1)
    c: Coincident(g1,g2)
    c: Coincident(g2,g3)
    c: Coincident(g3,g0)
    c: Horizontal(g0)
    c: Horizontal(g2)
    c: Vertical(g1)
    c: Vertical(g3)
    c: DistanceX(g0,g0) = 6
    c: DistanceY(g1,g0) = 12
    c: Coincident(g4,g5)
    c: Coincident(g5,g6)
    c: Coincident(g6,g7)
    c: Coincident(g7,g4)
    c: Horizontal(g4)
    c: Horizontal(g6)
    c: Vertical(g5)
    c: Vertical(g7)
    c: DistanceX(g4,g4) = 6
    c: DistanceY(g6,g4) = 12
    c: Vertical(g4,g1)
FEATURE [PartDesign::Pocket] Pocket
  BaseFeature = -> LinearPattern
  Direction = (-1,0,0)
  Length = 5
  Length2 = 5
  Profile = -> Sketch012
  ReferenceAxis = -> Sketch012 [N_Axis]
  Suppressed = false
  Type = 0
FEATURE [Sketcher::SketchObject] Sketch013  label="Tower Base Attahcment Holes Sketch"
  ArcFitTolerance = 1e-06
  AttachmentSupport = -> [DatumPlane]
  FullyConstrained = true
  MakeInternals = false
  MapMode = 5
  Placement = pos=(0,64.5,-1.43e-14) rot=(1,0,0;1.5708rad)
  expr: Constraints[0] = <<Monitor Chassis Parameters>>.GSM4TappingScrewHoleDiameter
  expr: Constraints[1] = <<Monitor Chassis Parameters>>.GSM4TappingScrewHoleDiameter
  expr: Constraints[3] = 0.5 * <<Monitor Chassis Parameters>>.GSCaseSlotRibHeight
  expr: Constraints[4] = <<Monitor Chassis Parameters>>.GSCaseSlotRibLength - 4 * <<Monitor Chassis Parameters>>.GSCaseSlotRibHeight
  expr: Constraints[5] = 0.5 * <<Monitor Chassis Parameters>>.GSCaseSlotRibLength - 2 * <<Monitor Chassis Parameters>>.GSCaseSlotRibHeight
  sketch-geometry (2):
    g0: Circle CenterX=20 CenterY=5 CenterZ=0 NormalX=0 NormalY=0 NormalZ=1 AngleXU=0 Radius=1.7
    g1: Circle CenterX=-20 CenterY=5 CenterZ=0 NormalX=0 NormalY=0 NormalZ=1 AngleXU=0 Radius=1.7
  constraints (6):
    c: Diameter(g0) = 3.4
    c: Diameter(g1) = 3.4
    c: Horizontal(g0,g1)
    c: DistanceY(g-1,g1) = 5
    c: DistanceX(g1,g0) = 40
    c: DistanceX(g1,g-1) = 20
FEATURE [PartDesign::Pocket] Pocket004  label="Tower Base Attahcment Holes Pocket"
  BaseFeature = -> Pocket
  Direction = (0,1,-2e-16)
  Length = 5
  Length2 = 5
  Profile = -> Sketch013
  ReferenceAxis = -> Sketch013 [N_Axis]
  Reversed = true
  Suppressed = false
  Type = 1
FEATURE [Sketcher::SketchObject] Sketch014  label="Lower Case Back Holes Sketch"
  ArcFitTolerance = 1e-06
  AttachmentSupport = -> [DatumPlane]
  FullyConstrained = false
  MakeInternals = false
  MapMode = 5
  Placement = pos=(0,64.5,-1.43e-14) rot=(1,0,0;1.5708rad)
  expr: Constraints[0] = <<Monitor Chassis Parameters>>.GSLowerBackCoverKnobHoleDiameter
  expr: Constraints[10] = <<Monitor Chassis Parameters>>.GSTowerCablePortWidth
  expr: Constraints[13] = 0.9 * <<Monitor Chassis Parameters>>.GSTowerCablePortWidth
  expr: Constraints[1] = <<Monitor Chassis Parameters>>.GSLowerBackCoverKnobHoleDiameter
  expr: Constraints[23] = <<Monitor Chassis Parameters>>.GSTowerCablePortWidth
  expr: Constraints[25] = 0.5 * <<Monitor Chassis Parameters>>.GSTowerCablePortWidth
  expr: Constraints[26] = 0.9 * <<Monitor Chassis Parameters>>.GSTowerCablePortWidth
  expr: Constraints[32] = 0.5 * <<Monitor Chassis Parameters>>.GSTowerCablePortWidth
  expr: Constraints[33] = 0.5 * <<Monitor Chassis Parameters>>.GSTowerCablePortWidth
  expr: Constraints[34] = 0.5 * <<Monitor Chassis Parameters>>.GSTowerCablePortWidth
  sketch-geometry (13):
    g0: Circle CenterX=-16.3077 CenterY=38.9762 CenterZ=0 NormalX=0 NormalY=0 NormalZ=1 AngleXU=0 Radius=7
    g1: Circle CenterX=-41.75 CenterY=38.9762 CenterZ=0 NormalX=0 NormalY=0 NormalZ=1 AngleXU=0 Radius=7
    g2: Circle CenterX=-44.9119 CenterY=102.252 CenterZ=0 NormalX=0 NormalY=0 NormalZ=1 AngleXU=0 Radius=2
    g3: LineSegment StartX=32 StartY=0 StartZ=0 EndX=52 EndY=0 EndZ=0
    g4: LineSegment StartX=52 StartY=0 StartZ=0 EndX=52 EndY=18 EndZ=0
    g5: LineSegment StartX=32 StartY=18 StartZ=0 EndX=32 EndY=0 EndZ=0
    g6: LineSegment StartX=-52 StartY=0 StartZ=0 EndX=-32 EndY=0 EndZ=0
    g7: LineSegment StartX=-32 StartY=0 StartZ=0 EndX=-32 EndY=18 EndZ=0
    g8: LineSegment StartX=-32 StartY=18 StartZ=0 EndX=-42 EndY=28 EndZ=0
    g9: LineSegment StartX=-42 StartY=28 StartZ=0 EndX=-52 EndY=18 EndZ=0
    g10: LineSegment StartX=-52 StartY=18 StartZ=0 EndX=-52 EndY=0 EndZ=0
    g11: LineSegment StartX=32 StartY=18 StartZ=0 EndX=42 EndY=28 EndZ=0
    g12: LineSegment StartX=42 StartY=28 StartZ=0 EndX=52 EndY=18 EndZ=0
  constraints (35):
    c: Diameter(g0) = 14
    c: Diameter(g1) = 14
    c: Horizontal(g0,g1)
    c: Diameter(g2) = 4
    c: PointOnObject(g3,g-1)
    c: PointOnObject(g3,g-1)
    c: Coincident(g4,g3)
    c: Vertical(g4)
    c: Coincident(g5,g3)
    c: Vertical(g5)
    c: DistanceX(g3,g3) = 20
    c: DistanceX(g1,g-1) = 41.75
    c: Horizontal(g5,g4)
    c: DistanceY(g3,g5) = 18
    c: PointOnObject(g6,g-1)
    c: PointOnObject(g6,g-1)
    c: Coincident(g7,g6)
    c: Vertical(g7)
    c: Coincident(g8,g7)
    c: Coincident(g9,g8)
    c: Coincident(g10,g9)
    c: Coincident(g10,g6)
    c: Vertical(g10)
    c: DistanceX(g6,g6) = 20
    c: Horizontal(g9,g7)
    c: DistanceY(g9,g8) = 10
    c: DistanceY(g6,g9) = 18
    c: Coincident(g11,g5)
    c: Coincident(g12,g11)
    c: Coincident(g12,g4)
    c: DistanceX(g6,g-1) = 32
    c: DistanceX(g-1,g3) = 32
    c: DistanceX(g5,g11) = 10
    c: DistanceY(g5,g11) = 10
    c: DistanceX(g9,g8) = 10
FEATURE [PartDesign::Pocket] Pocket005  label="Lower Case Back Holes Pocket"
  BaseFeature = -> Pocket004
  Direction = (0,1,-2e-16)
  Length = 5
  Length2 = 5
  Profile = -> Sketch014
  ReferenceAxis = -> Sketch014 [N_Axis]
  Reversed = true
  Suppressed = false
  Type = 0
FEATURE [PartDesign::Body] Body  label="Lower Case Cover Body"
  AllowCompound = false
  Group = -> [Sketch,Pad,Sketch001,Pad001,Mirrored,DatumPlane,DatumPlane001,Sketch003,Pad002,Sketch004,Pad003,DatumPlane003,Sketch009,Pocket001,LinearPattern,Sketch012,Pocket,Sketch013,Pocket004,Sketch014,Pocket005]
  Origin = -> Origin001
  Placement = pos=(1.4,0,0) rot=(0,0,1;0rad)
  Tip = -> Pocket005
FEATURE [PartDesign::Plane] DatumPlane005  label="Case Top Back DatumPlane"
  AttachmentOffset = pos=(0,0,-64.5) rot=(0,0,1;0rad)
  AttachmentSupport = -> [XZ_Plane002]
  Length = 159.723
  MapMode = 5
  Placement = pos=(0,64.5,-1.43e-14) rot=(1,0,0;1.5708rad)
  ResizeMode = 0
  Width = 282.636
  expr: .AttachmentOffset.Base.z = -(0.5 * <<Monitor Chassis Parameters>>.GSCaseWallInnerDepth + <<Monitor Chassis Parameters>>.GSCaseWallThickness)
FEATURE [Sketcher::SketchObject] Sketch015  label="Case Top Back Access Holes Sketch"
  ArcFitTolerance = 1e-06
  AttachmentSupport = -> [DatumPlane005]
  ExternalGeometry = -> [Sketch010]
  FullyConstrained = false
  MakeInternals = false
  MapMode = 5
  Placement = pos=(0,64.5,-1.43e-14) rot=(1,0,0;1.5708rad)
  expr: Constraints[52] = <<Monitor Chassis Parameters>>.GSCaseCoverBackCoolingSlotSeparation
  expr: Constraints[53] = <<Monitor Chassis Parameters>>.GSCaseCoverBackCoolingSlotSeparation
  expr: Constraints[54] = <<Monitor Chassis Parameters>>.GSCaseCoverBackCoolingSlotSeparation
  sketch-geometry (17):
    g0: Circle CenterX=-45.0354 CenterY=71.0638 CenterZ=0 NormalX=0 NormalY=0 NormalZ=1 AngleXU=0 Radius=2
    g1: LineSegment StartX=-27.3223 StartY=78.3837 StartZ=0 EndX=-27.3223 EndY=133 EndZ=0
    g2: LineSegment StartX=-23.3223 StartY=133 StartZ=0 EndX=-23.3223 EndY=78.3837 EndZ=0
    g3: ArcOfCircle CenterX=-25.3223 CenterY=78.3837 CenterZ=0 NormalX=0 NormalY=0 NormalZ=1 AngleXU=0 Radius=2 StartAngle=3.14159 EndAngle=6.28319
    g4: ArcOfCircle CenterX=-25.3223 CenterY=133 CenterZ=0 NormalX=0 NormalY=0 NormalZ=1 AngleXU=0 Radius=2 StartAngle=0 EndAngle=3.14159
    g5: LineSegment StartX=-12.3223 StartY=78.3837 StartZ=0 EndX=-12.3223 EndY=133 EndZ=0
    g6: LineSegment StartX=-8.32227 StartY=133 StartZ=0 EndX=-8.32227 EndY=78.3837 EndZ=0
    g7: ArcOfCircle CenterX=-10.3223 CenterY=78.3837 CenterZ=0 NormalX=0 NormalY=0 NormalZ=1 AngleXU=0 Radius=2 StartAngle=3.14159 EndAngle=6.28319
    g8: ArcOfCircle CenterX=-10.3223 CenterY=133 CenterZ=0 NormalX=0 NormalY=0 NormalZ=1 AngleXU=0 Radius=2 StartAngle=0 EndAngle=3.14159
    g9: LineSegment StartX=2.67773 StartY=78.3837 StartZ=0 EndX=2.67773 EndY=133 EndZ=0
    g10: LineSegment StartX=6.67773 StartY=133 StartZ=0 EndX=6.67773 EndY=78.3837 EndZ=0
    g11: ArcOfCircle CenterX=4.67773 CenterY=78.3837 CenterZ=0 NormalX=0 NormalY=0 NormalZ=1 AngleXU=0 Radius=2 StartAngle=3.14159 EndAngle=6.28319
    g12: ArcOfCircle CenterX=4.67773 CenterY=133 CenterZ=0 NormalX=0 NormalY=0 NormalZ=1 AngleXU=0 Radius=2 StartAngle=0 EndAngle=3.14159
    g13: LineSegment StartX=-42.3223 StartY=78.3837 StartZ=0 EndX=-42.3223 EndY=133 EndZ=0
    g14: LineSegment StartX=-38.3223 StartY=133 StartZ=0 EndX=-38.3223 EndY=78.3837 EndZ=0
    g15: ArcOfCircle CenterX=-40.3223 CenterY=78.3837 CenterZ=0 NormalX=0 NormalY=0 NormalZ=1 AngleXU=0 Radius=2 StartAngle=3.14159 EndAngle=6.28319
    g16: ArcOfCircle CenterX=-40.3223 CenterY=133 CenterZ=0 NormalX=0 NormalY=0 NormalZ=1 AngleXU=0 Radius=2 StartAngle=0 EndAngle=3.14159
  constraints (55):
    c: Diameter(g0) = 4
    c: Vertical(g1)
    c: Vertical(g2)
    c: Horizontal(g1,g2)
    c: Horizontal(g2,g1)
    c: DistanceY(g-1,g2) = 133
    c: DistanceX(g1,g2) = 4
    c: Coincident(g3,g1)
    c: Coincident(g3,g2)
    c: Horizontal(g3,g2)
    c: Coincident(g4,g1)
    c: Coincident(g4,g2)
    c: Horizontal(g4,g2)
    c: Vertical(g5)
    c: Vertical(g6)
    c: Horizontal(g5,g6)
    c: Horizontal(g6,g5)
    c: DistanceY(g-1,g6) = 133
    c: DistanceX(g5,g6) = 4
    c: Coincident(g7,g5)
    c: Coincident(g7,g6)
    c: Horizontal(g7,g6)
    c: Coincident(g8,g5)
    c: Coincident(g8,g6)
    c: Horizontal(g8,g6)
    c: Vertical(g9)
    c: Vertical(g10)
    c: Horizontal(g9,g10)
    c: Horizontal(g10,g9)
    c: DistanceY(g-1,g10) = 133
    c: DistanceX(g9,g10) = 4
    c: Coincident(g11,g9)
    c: Coincident(g11,g10)
    c: Horizontal(g11,g10)
    c: Coincident(g12,g9)
    c: Coincident(g12,g10)
    c: Horizontal(g12,g10)
    c: Vertical(g13)
    c: Vertical(g14)
    c: Horizontal(g13,g14)
    c: Horizontal(g14,g13)
    c: DistanceY(g-1,g14) = 133
    c: DistanceX(g13,g14) = 4
    c: Coincident(g15,g13)
    c: Coincident(g15,g14)
    c: Horizontal(g15,g14)
    c: Coincident(g16,g13)
    c: Coincident(g16,g14)
    c: Horizontal(g16,g14)
    c: Horizontal(g15,g3)
    c: Horizontal(g3,g7)
    c: Horizontal(g7,g11)
    c: DistanceX(g15,g3) = 15
    c: DistanceX(g3,g7) = 15
    c: DistanceX(g7,g11) = 15
FEATURE [PartDesign::Pocket] Pocket006  label="Case Top Back Access Holes Pocket"
  BaseFeature = -> LinearPattern002
  Direction = (0,1,-2e-16)
  Length = 5
  Length2 = 5
  Profile = -> Sketch015
  ReferenceAxis = -> Sketch015 [N_Axis]
  Reversed = true
  Suppressed = false
  Type = 0
FEATURE [Sketcher::SketchObject] Sketch016  label="Case Top Right Side Access Holes Sketch"
  ArcFitTolerance = 1e-06
  AttachmentSupport = -> [DatumPlane004]
  FullyConstrained = false
  MakeInternals = false
  MapMode = 5
  Placement = pos=(62.3,0,0) rot=(0.57735,0.57735,0.57735;2.0944rad)
  expr: Constraints[16] = <<Monitor Chassis Parameters>>.GSLUSBStackAccesshHoleWidth
  expr: Constraints[17] = <<Monitor Chassis Parameters>>.GSLUSBStackAccesshHoleLength
  sketch-geometry (12):
    g0: LineSegment StartX=35.4573 StartY=26.6809 StartZ=0 EndX=35.4573 EndY=8.81649 EndZ=0
    g1: LineSegment StartX=35.4573 StartY=8.81649 StartZ=0 EndX=47.8938 EndY=8.81649 EndZ=0
    g2: LineSegment StartX=47.8938 StartY=8.81649 StartZ=0 EndX=47.8938 EndY=26.6809 EndZ=0
    g3: LineSegment StartX=47.8938 StartY=26.6809 StartZ=0 EndX=35.4573 EndY=26.6809 EndZ=0
    g4: LineSegment StartX=34.4071 StartY=73.3002 StartZ=0 EndX=34.4071 EndY=53.3002 EndZ=0
    g5: LineSegment StartX=34.4071 StartY=53.3002 StartZ=0 EndX=54.4071 EndY=53.3002 EndZ=0
    g6: LineSegment StartX=54.4071 StartY=53.3002 StartZ=0 EndX=54.4071 EndY=73.3002 EndZ=0
    g7: LineSegment StartX=54.4071 StartY=73.3002 StartZ=0 EndX=34.4071 EndY=73.3002 EndZ=0
    g8: LineSegment StartX=34.2792 StartY=140.745 StartZ=0 EndX=34.2792 EndY=120.745 EndZ=0
    g9: LineSegment StartX=34.2792 StartY=120.745 StartZ=0 EndX=54.2792 EndY=120.745 EndZ=0
    g10: LineSegment StartX=54.2792 StartY=120.745 StartZ=0 EndX=54.2792 EndY=140.745 EndZ=0
    g11: LineSegment StartX=54.2792 StartY=140.745 StartZ=0 EndX=34.2792 EndY=140.745 EndZ=0
  constraints (28):
    c: Coincident(g0,g1)
    c: Coincident(g1,g2)
    c: Coincident(g2,g3)
    c: Coincident(g3,g0)
    c: Vertical(g0)
    c: Vertical(g2)
    c: Horizontal(g1)
    c: Horizontal(g3)
    c: Coincident(g4,g5)
    c: Coincident(g5,g6)
    c: Coincident(g6,g7)
    c: Coincident(g7,g4)
    c: Vertical(g4)
    c: Vertical(g6)
    c: Horizontal(g5)
    c: Horizontal(g7)
    c: DistanceX(g4,g6) = 20
    c: DistanceY(g4,g4) = 20
    c: Coincident(g8,g9)
    c: Coincident(g9,g10)
    c: Coincident(g10,g11)
    c: Coincident(g11,g8)
    c: Vertical(g8)
    c: Vertical(g10)
    c: Horizontal(g9)
    c: Horizontal(g11)
    c: DistanceX(g8,g10) = 20
    c: DistanceY(g8,g8) = 20
FEATURE [PartDesign::Pocket] Pocket008  label="Case Top Right Side Access Holes Pocket"
  BaseFeature = -> Pocket006
  Direction = (-1,0,0)
  Length = 5
  Length2 = 5
  Profile = -> Sketch016
  ReferenceAxis = -> Sketch016 [N_Axis]
  Suppressed = false
  Type = 0
FEATURE [Sketcher::SketchObject] Sketch017  label="Right Side Rib Stabilization Sketch"
  ArcFitTolerance = 1e-06
  AttachmentSupport = -> [DatumPlane004]
  FullyConstrained = false
  MakeInternals = false
  MapMode = 5
  Placement = pos=(62.3,0,0) rot=(0.57735,0.57735,0.57735;2.0944rad)
  expr: Constraints[12] = <<Monitor Chassis Parameters>>.GSBasePowerBoxCoolingSlotWidth
  expr: Constraints[6] = <<Monitor Chassis Parameters>>.GSBasePowerBoxCoolingSlotWidth
  sketch-geometry (8):
    g0: LineSegment StartX=55.7945 StartY=119.712 StartZ=0 EndX=-56.9644 EndY=30.8875 EndZ=0
    g1: LineSegment StartX=-56.9644 StartY=30.8875 StartZ=0 EndX=-56.9644 EndY=27.8875 EndZ=0
    g2: LineSegment StartX=-56.9644 StartY=27.8875 StartZ=0 EndX=55.7945 EndY=116.712 EndZ=0
    g3: LineSegment StartX=55.7945 StartY=116.712 StartZ=0 EndX=55.7945 EndY=119.712 EndZ=0
    g4: LineSegment StartX=54.0673 StartY=31.3418 StartZ=0 EndX=-55.9764 EndY=119.712 EndZ=0
    g5: LineSegment StartX=-55.9764 StartY=119.712 StartZ=0 EndX=-55.9764 EndY=116.712 EndZ=0
    g6: LineSegment StartX=-55.9764 StartY=116.712 StartZ=0 EndX=54.0673 EndY=27.8875 EndZ=0
    g7: LineSegment StartX=54.0673 StartY=27.8875 StartZ=0 EndX=54.0673 EndY=31.3418 EndZ=0
  constraints (17):
    c: Coincident(g1,g0)
    c: Coincident(g2,g1)
    c: Coincident(g3,g2)
    c: Coincident(g3,g0)
    c: Parallel(g2,g0)
    c: Parallel(g1,g3)
    c: DistanceY(g1,g0) = 3
    c: Coincident(g5,g4)
    c: Coincident(g6,g5)
    c: Coincident(g7,g6)
    c: Coincident(g7,g4)
    c: Vertical(g1,g0)
    c: DistanceY(g5,g4) = 3
    c: Vertical(g5,g4)
    c: Vertical(g6,g4)
    c: Horizontal(g6,g1)
    c: Horizontal(g4,g0)
FEATURE [PartDesign::Pad] Pad007  label="Right Side Rib Stabilization Pad"
  BaseFeature = -> Pocket008
  Direction = (1,0,0)
  Length = 3
  Length2 = 10
  Profile = -> Sketch017
  ReferenceAxis = -> Sketch017 [N_Axis]
  Reversed = true
  Suppressed = false
  Type = 0
  expr: Length = <<Monitor Chassis Parameters>>.GSCaseWallThickness
FEATURE [PartDesign::Plane] DatumPlane006  label="Upper Cover Right Side DatumPlane001"
  AttachmentOffset = pos=(0,0,62.3) rot=(0,0,1;0rad)
  AttachmentSupport = -> [YZ_Plane002]
  Length = 379.056
  MapMode = 5
  Placement = pos=(62.3,0,0) rot=(0.57735,0.57735,0.57735;2.0944rad)
  ResizeMode = 0
  Width = 1743.28
  expr: .AttachmentOffset.Base.z = 0.5 * <<Monitor Chassis Parameters>>.GSCaseWallInnerWidth + <<Monitor Chassis Parameters>>.GSCaseWallThickness
FEATURE [PartDesign::Plane] DatumPlane007  label="Upper Cover Left Side DatumPlane"
  AttachmentOffset = pos=(0,0,-62.3) rot=(0,0,1;0rad)
  AttachmentSupport = -> [YZ_Plane002]
  Length = 161.319
  MapMode = 2
  Placement = pos=(-62.3,0,0) rot=(0.57735,0.57735,0.57735;2.0944rad)
  ResizeMode = 0
  Width = 282.833
  expr: .AttachmentOffset.Base.z = -0.5 * <<Monitor Chassis Parameters>>.GSCaseWallInnerWidth - <<Monitor Chassis Parameters>>.GSCaseWallThickness
FEATURE [Sketcher::SketchObject] Sketch018  label="Left Side Rib Stabilization Sketch"
  ArcFitTolerance = 1e-06
  AttachmentSupport = -> [DatumPlane007]
  FullyConstrained = false
  MakeInternals = false
  MapMode = 5
  Placement = pos=(-62.3,0,0) rot=(0.57735,0.57735,0.57735;2.0944rad)
  sketch-geometry (8):
    g0: LineSegment StartX=55.7945 StartY=119.712 StartZ=0 EndX=-56.9644 EndY=30.8875 EndZ=0
    g1: LineSegment StartX=-56.9644 StartY=30.8875 StartZ=0 EndX=-56.9644 EndY=27.8875 EndZ=0
    g2: LineSegment StartX=-56.9644 StartY=27.8875 StartZ=0 EndX=55.7945 EndY=116.712 EndZ=0
    g3: LineSegment StartX=55.7945 StartY=116.712 StartZ=0 EndX=55.7945 EndY=119.712 EndZ=0
    g4: LineSegment StartX=54.0673 StartY=31.3418 StartZ=0 EndX=-55.9764 EndY=119.712 EndZ=0
    g5: LineSegment StartX=-55.9764 StartY=119.712 StartZ=0 EndX=-55.9764 EndY=116.712 EndZ=0
    g6: LineSegment StartX=-55.9764 StartY=116.712 StartZ=0 EndX=54.0673 EndY=27.8875 EndZ=0
    g7: LineSegment StartX=54.0673 StartY=27.8875 StartZ=0 EndX=54.0673 EndY=31.3418 EndZ=0
  constraints (17):
    c: Coincident(g1,g0)
    c: Coincident(g2,g1)
    c: Coincident(g3,g2)
    c: Coincident(g3,g0)
    c: Parallel(g2,g0)
    c: Parallel(g1,g3)
    c: DistanceY(g1,g0) = 3
    c: Coincident(g5,g4)
    c: Coincident(g6,g5)
    c: Coincident(g7,g6)
    c: Coincident(g7,g4)
    c: Vertical(g1,g0)
    c: DistanceY(g5,g4) = 3
    c: Vertical(g5,g4)
    c: Vertical(g6,g4)
    c: Horizontal(g6,g1)
    c: Horizontal(g4,g0)
FEATURE [PartDesign::Pad] Pad008  label="Right Side Rib Stabilization Pad001"
  BaseFeature = -> Pad007
  Direction = (1,0,0)
  Length = 3
  Length2 = 10
  Profile = -> Sketch018
  ReferenceAxis = -> Sketch018 [N_Axis]
  Suppressed = false
  Type = 0
  expr: Length = <<Monitor Chassis Parameters>>.GSCaseWallThickness
FEATURE [PartDesign::Body] Body001  label="Upper Case Cover Body"
  AllowCompound = false
  Group = -> [Sketch006,Pad004,DatumPlane002,Sketch007,Sketch008,Pad005,Mirrored001,Pad006,DatumPlane004,Sketch010,Pocket002,LinearPattern001,Sketch011,Pocket003,LinearPattern002,DatumPlane005,Sketch015,Pocket006,Sketch016,Pocket008,Sketch017,Pad007,DatumPlane007,Sketch018,Pad008]
  Origin = -> Origin002
  Placement = pos=(1.4,0,110.1) rot=(0,0,1;0rad)
  Tip = -> Pad008
FEATURE [App::Part] Part  label="Case Cover Part"
  Group = -> [Body,Body001]
  Origin = -> Origin
  Placement = pos=(0.3,0,0) rot=(0,0,1;0rad)
---- part ../Tower/Tower.FCStd = doc fcstd_a32997a933d4 (72997 chars; too large to inline — full recipe in that document) ----
